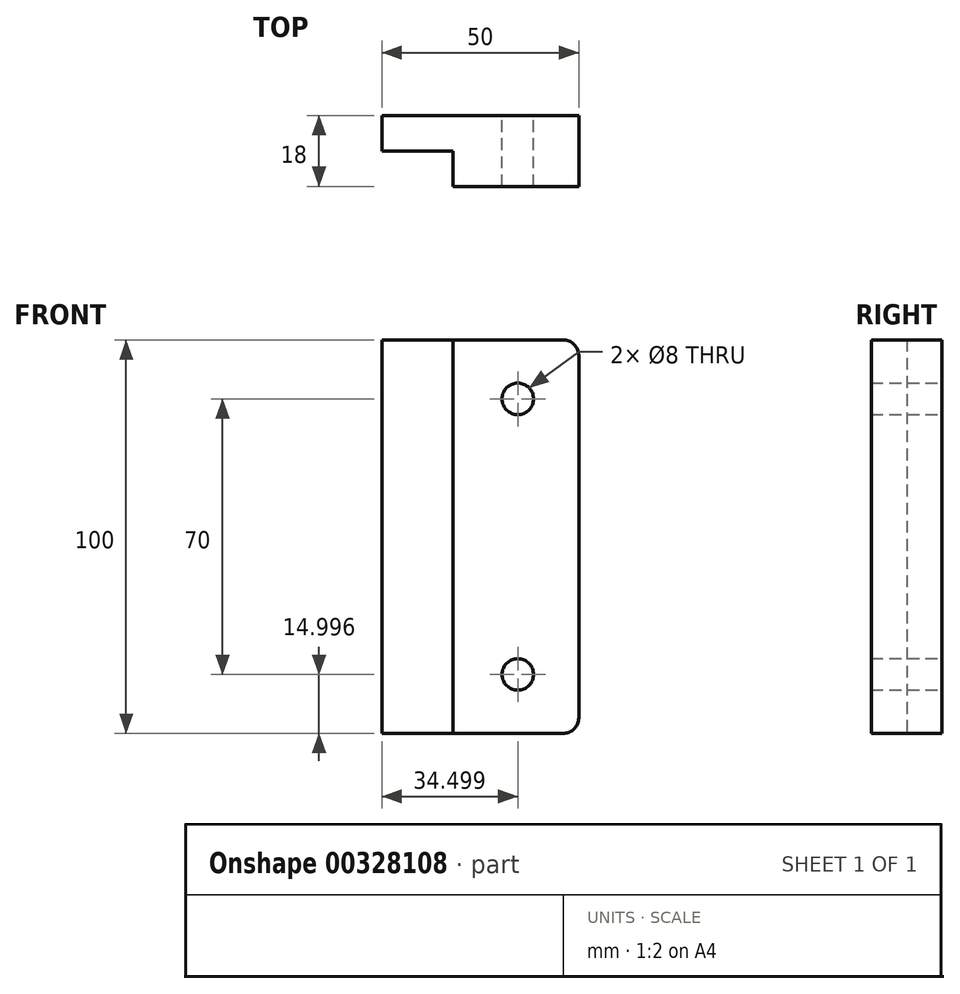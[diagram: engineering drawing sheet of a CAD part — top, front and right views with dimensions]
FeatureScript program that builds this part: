
annotation { "Feature Type Name" : "Feature", "Feature Type Description" : "" }
export const myFeature = defineFeature(function(context is Context, id is Id, definition is map)
    precondition{}
    {
        {
            var Q0;
            Q0=qCreatedBy(makeId("Front.planeOp"),FACE);
            var sketch = newSketch(context, id + "F0", { "sketchPlane" : qUnion([Q0])});
            skLineSegment(sketch, "E0", {"start": v(-59.24, 115.12) * mm, "end": v(-59.24, 23.12) * mm});
            skArc(sketch, "E1", {"start": v(-59.24, 23.12) * mm, "mid": v(-60.41, 20.29) * mm, "end": v(-63.24, 19.12) * mm});
            skLineSegment(sketch, "E2", {"start": v(-63.24, 19.12) * mm, "end": v(-109.24, 19.12) * mm});
            skLineSegment(sketch, "E3", {"start": v(-109.24, 19.12) * mm, "end": v(-109.24, 119.12) * mm});
            skLineSegment(sketch, "E4", {"start": v(-109.24, 119.12) * mm, "end": v(-63.24, 119.12) * mm});
            skArc(sketch, "E5", {"start": v(-63.24, 119.12) * mm, "mid": v(-60.41, 117.94) * mm, "end": v(-59.24, 115.12) * mm});
            skCircle(sketch, "E6", {"center": v(-74.74, 104.12) * mm, "radius": 4 * mm});
            skCircle(sketch, "E7", {"center": v(-74.74, 34.12) * mm, "radius": 4 * mm});
            skLineSegment(sketch, "E8", {"start": v(-95.24, 9.12) * mm, "end": v(-115.24, 9.12) * mm});
            skArc(sketch, "E9", {"start": v(-115.24, 9.12) * mm, "mid": v(-118.07, 10.29) * mm, "end": v(-119.24, 13.12) * mm});
            skLineSegment(sketch, "E10", {"start": v(-119.24, 13.12) * mm, "end": v(-119.24, 125.12) * mm});
            skArc(sketch, "E11", {"start": v(-119.24, 125.12) * mm, "mid": v(-118.07, 127.94) * mm, "end": v(-115.24, 129.12) * mm});
            skLineSegment(sketch, "E12", {"start": v(-115.24, 129.12) * mm, "end": v(-95.24, 129.12) * mm});
            skArc(sketch, "E13", {"start": v(-95.24, 129.12) * mm, "mid": v(-92.41, 127.94) * mm, "end": v(-91.24, 125.12) * mm});
            skLineSegment(sketch, "E14", {"start": v(-91.24, 125.12) * mm, "end": v(-91.24, 13.12) * mm});
            skArc(sketch, "E15", {"start": v(-91.24, 13.12) * mm, "mid": v(-92.41, 10.29) * mm, "end": v(-95.24, 9.12) * mm});
            skSolve(sketch);
        }
        {
            var Q0;
            Q0=makeQuery(id+"F0.imprint","IMPRINT",FACE,{"disambiguationData":[TD([[makeQuery(id+"F0.imprint","IMPRINT",EDGE,{"derivedFrom":sQuery(id+"F0.wireOp",EDGE,"E0")}),-1.0]])]});
            extrude(context, id + "F1", {"entities" : qUnion([Q0]), "depth" : 18 * mm});
        }
        {
            var Q0;
            {var subQ0=sQuery(id+"F0.wireOp",EDGE,"E3");Q0=makeQuery(id+"F0.imprint","IMPRINT",FACE,{"disambiguationData":[TD([[makeQuery(id+"F0.imprint","IMPRINT",EDGE,{"derivedFrom":subQ0}),-1.0]])]});}
            extrude(context, id + "F2", {"entities" : qUnion([Q0]), "operationType" : NewBodyOperationType.ADD, "depth" : 9 * mm});
        }
    });
